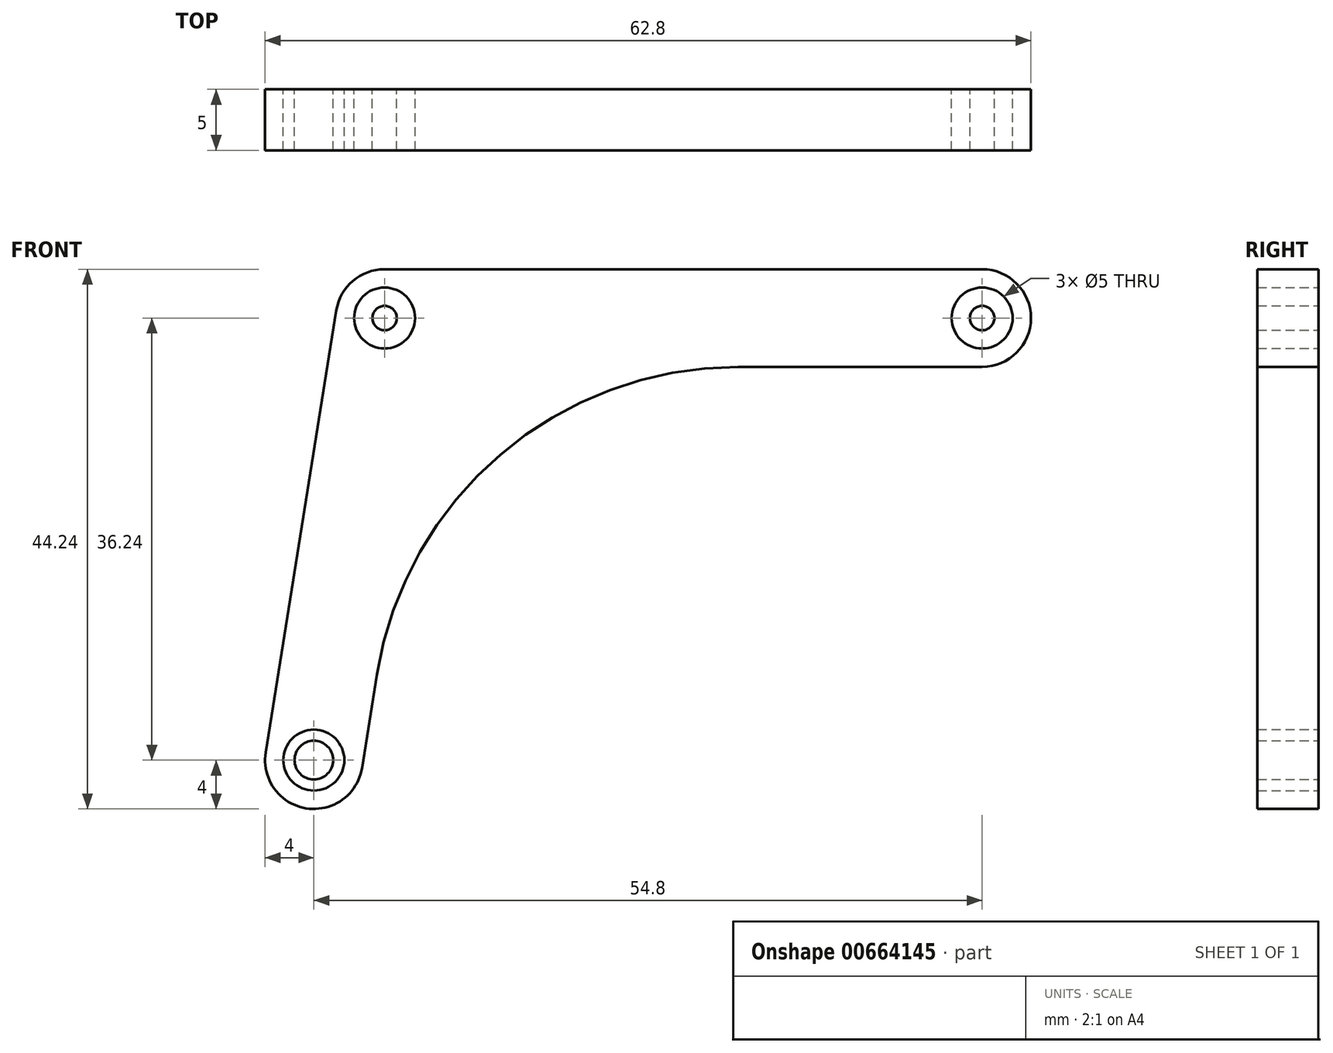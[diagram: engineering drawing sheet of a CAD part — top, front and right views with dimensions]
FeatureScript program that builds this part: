
annotation { "Feature Type Name" : "Feature", "Feature Type Description" : "" }
export const myFeature = defineFeature(function(context is Context, id is Id, definition is map)
    precondition{}
    {
        {
            var Q0;
            Q0=qCreatedBy(makeId("Front.planeOp"),FACE);
            var sketch = newSketch(context, id + "F0", { "sketchPlane" : qUnion([Q0])});
            skCircle(sketch, "E0", {"center": v(0, 0) * mm, "radius": 2.5 * mm});
            skArc(sketch, "E1", {"start": v(0, 4) * mm, "mid": v(-2.6, 3.04) * mm, "end": v(-3.95, 0.63) * mm});
            skArc(sketch, "E2", {"start": v(-9.75, -35.6) * mm, "mid": v(-6.43, -40.19) * mm, "end": v(-1.85, -36.87) * mm});
            skLineSegment(sketch, "E3", {"start": v(-3.95, 0.63) * mm, "end": v(-9.75, -35.6) * mm});
            skArc(sketch, "E4", {"start": v(49, -4) * mm, "mid": v(53, 0) * mm, "end": v(49, 4) * mm});
            skLineSegment(sketch, "E5", {"start": v(0, 4) * mm, "end": v(49, 4) * mm});
            skLineSegment(sketch, "E6.0", {"start": v(29, -4) * mm, "end": v(49, -4) * mm});
            skLineSegment(sketch, "E7.0", {"start": v(-0.63, -29.26) * mm, "end": v(-1.85, -36.87) * mm});
            skPoint(sketch, "E8.visualSharp", {"position": v(3.41, -4) * mm});
            skArc(sketch, "E8.filletArc", {"start": v(29, -4) * mm, "mid": v(9.53, -11.17) * mm, "end": v(-0.63, -29.26) * mm});
            skCircle(sketch, "E9", {"center": v(-5.8, -36.24) * mm, "radius": 2.5 * mm});
            skCircle(sketch, "E10", {"center": v(49, 0) * mm, "radius": 2.5 * mm});
            skSolve(sketch);
        }
        {
            var Q0;
            Q0 = qSketchRegion(id + "F0", true);
            extrude(context, id + "F1", {"entities" : qUnion([Q0]), "depth" : 5 * mm, "offsetDistance" : 25 * mm});
        }
        {
            var Q0;
            Q0=qCreatedBy(makeId("Front.planeOp"),FACE);
            var sketch = newSketch(context, id + "F2", { "sketchPlane" : qUnion([Q0])});
            skCircle(sketch, "E11.0", {"center": v(-5.8, -36.24) * mm, "radius": 2.5 * mm, "construction": true});
            skCircle(sketch, "E12.0", {"center": v(0, 0) * mm, "radius": 2.5 * mm, "construction": true});
            skCircle(sketch, "E13.0", {"center": v(49, 0) * mm, "radius": 2.5 * mm, "construction": true});
            skCircle(sketch, "E14", {"center": v(0, 0) * mm, "radius": 1 * mm});
            skCircle(sketch, "E15", {"center": v(-5.8, -36.24) * mm, "radius": 1.58 * mm});
            skCircle(sketch, "E16", {"center": v(49, 0) * mm, "radius": 1 * mm});
            skSolve(sketch);
        }
        {
            var Q0;
            Q0 = qSketchRegion(id + "F2", true);
            extrude(context, id + "F3", {"entities" : qUnion([Q0]), "depth" : 5 * mm, "offsetDistance" : 25 * mm});
        }
    });
